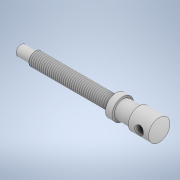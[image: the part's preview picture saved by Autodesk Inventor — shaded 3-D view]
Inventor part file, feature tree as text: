
AUTODESK INVENTOR PART (.ipt)
format: ipt  version: 2021 (Build 250183000, 183)  size: 143,360 bytes
history: native  units: mm
features: other x2, sketch x2, thread x1, extrude x1
ambient origin geometry x8: Origin, YZ Plane, XZ Plane, XY Plane, X Axis, Y Axis, Z Axis, Center Point
bodies: Body1 (feature_tree)
feature tree (6):
  other  "Sólido1"
  other  "Revolução1"
  thread  "Rosca1"  [1 undecoded]
  extrude  "Extrusão1"  Depth=1.25mm
  sketch  "Esboço1"  dims[d15=10.297443mm d17=1.25mm]
  sketch  "Esboço3"  dims[d19=3.0mm d20=5.0mm d21=12.0mm d22=15.0mm d24=13.0mm d25=1.5mm d26=7.5mm d27=90.0deg d28=65.0mm d29=0.0mm d30=6.5mm d34=7.0mm d35=8.0mm d36=0.0mm d37=34.0mm d33=0.5mm]
note: 1 required parameter value undecoded (feature->parameter linkage not recoverable at this tier; creation-order binding heuristic only, values carry confidence <= 0.55)
